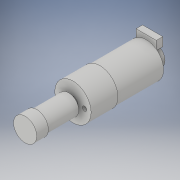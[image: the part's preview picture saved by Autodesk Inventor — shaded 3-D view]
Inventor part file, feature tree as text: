
AUTODESK INVENTOR PART (.ipt)
format: ipt  version: 2018.2 (Build 222227000, 227)  size: 155,648 bytes
history: native  units: in
note: dims shown in document units (in); Inventor stores cm internally (conversion verified against a paired STEP export)
features: sketch x9, extrude x8
ambient origin geometry x8: Origin, YZ Plane, XZ Plane, XY Plane, X Axis, Y Axis, Z Axis, Center Point
bodies: Solid1 (feature_tree)
feature tree (17):
  extrude  "Extrusion1"  Depth=1.2598in TaperAngle=0.0deg
  sketch  "Sketch2"  dims[d3=0.9843in d4=0.7283in d5=0.0in]
  sketch  "Sketch3"  dims[d6=0.2756in d7=0.1181in d8=0.0in]
  extrude  "Extrusion2"  Depth=0.7283in TaperAngle=0.0deg
  extrude  "Extrusion3"  Depth=0.1181in TaperAngle=0.0deg
  extrude  "Extrusion6"  Depth=0.2362in TaperAngle=0.0deg
  extrude  "Extrusion7"  Depth=0.5512in
  extrude  "Extrusion8"  Depth=0.1181in
  extrude  "Extrusion9"  Depth=0.1181in
  extrude  "Extrusion10"  Depth=0.1969in TaperAngle=0.0deg
  sketch  "Sketch1"  dims[d0=0.9449in d1=1.2598in d2=0.0in]
  sketch  "Sketch4"  dims[d15=0.5512in d16=0.2362in d17=0.0in]
  sketch  "Sketch7"  dims[d20=0.2756in d21=0.5512in]
  sketch  "Sketch8"  dims[d22=0.1772in d23=0.0in d24=0.1181in]
  sketch  "Sketch9"  dims[d25=0.315in d26=0.1181in]
  sketch  "Sketch10"  dims[d27=0.315in d28=0.1969in d29=0.0in]
  sketch  "Sketch11"  dims[d30=0.5512in d31=0.8661in d32=0.0in d33=0.6299in d34=0.315in d35=0.0in]
